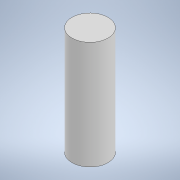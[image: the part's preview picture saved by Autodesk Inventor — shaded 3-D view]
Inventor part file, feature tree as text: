
AUTODESK INVENTOR PART (.ipt)
format: ipt  version: 2021 (Build 250183000, 183)  size: 90,624 bytes
history: native  units: in
note: dims shown in document units (in); Inventor stores cm internally (conversion verified against a paired STEP export)
features: extrude x1, sketch x1
ambient origin geometry x8: Origin, YZ Plane, XZ Plane, XY Plane, X Axis, Y Axis, Z Axis, Center Point
bodies: Solid1 (feature_tree)
feature tree (2):
  extrude  "Extrusion1"  Depth=3.0in TaperAngle=0.0deg
  sketch  "Sketch1"  dims[d0=1.0in d1=3.0in d2=0.0in]
